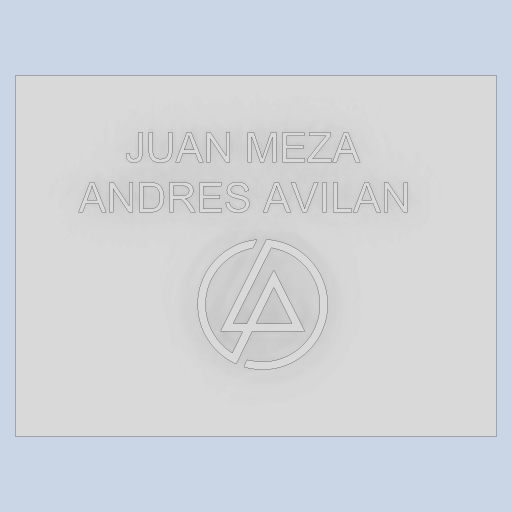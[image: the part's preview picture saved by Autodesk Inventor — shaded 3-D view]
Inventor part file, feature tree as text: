
AUTODESK INVENTOR PART (.ipt)
format: ipt  version: 2024 (Build 280153000, 153)  size: 2,998,784 bytes
history: native  units: mm
features: extrude x2, sketch x2, other x1
ambient origin geometry x8: Origin, YZ Plane, XZ Plane, XY Plane, X Axis, Y Axis, Z Axis, Center Point
bodies: Body1 (feature_tree)
feature tree (5):
  other  "Sólido1"
  extrude  "Extrusión1"  Depth=400.0mm
  extrude  "Extrusión2"  Depth=400.0mm
  sketch  "Boceto1"  dims[d0=300.0mm d1=400.0mm]
  sketch  "Boceto2"  dims[d2=10.0mm d3=0.0mm d4=400.0mm d5=300.0mm d6=100.0mm d7=0.0mm]
